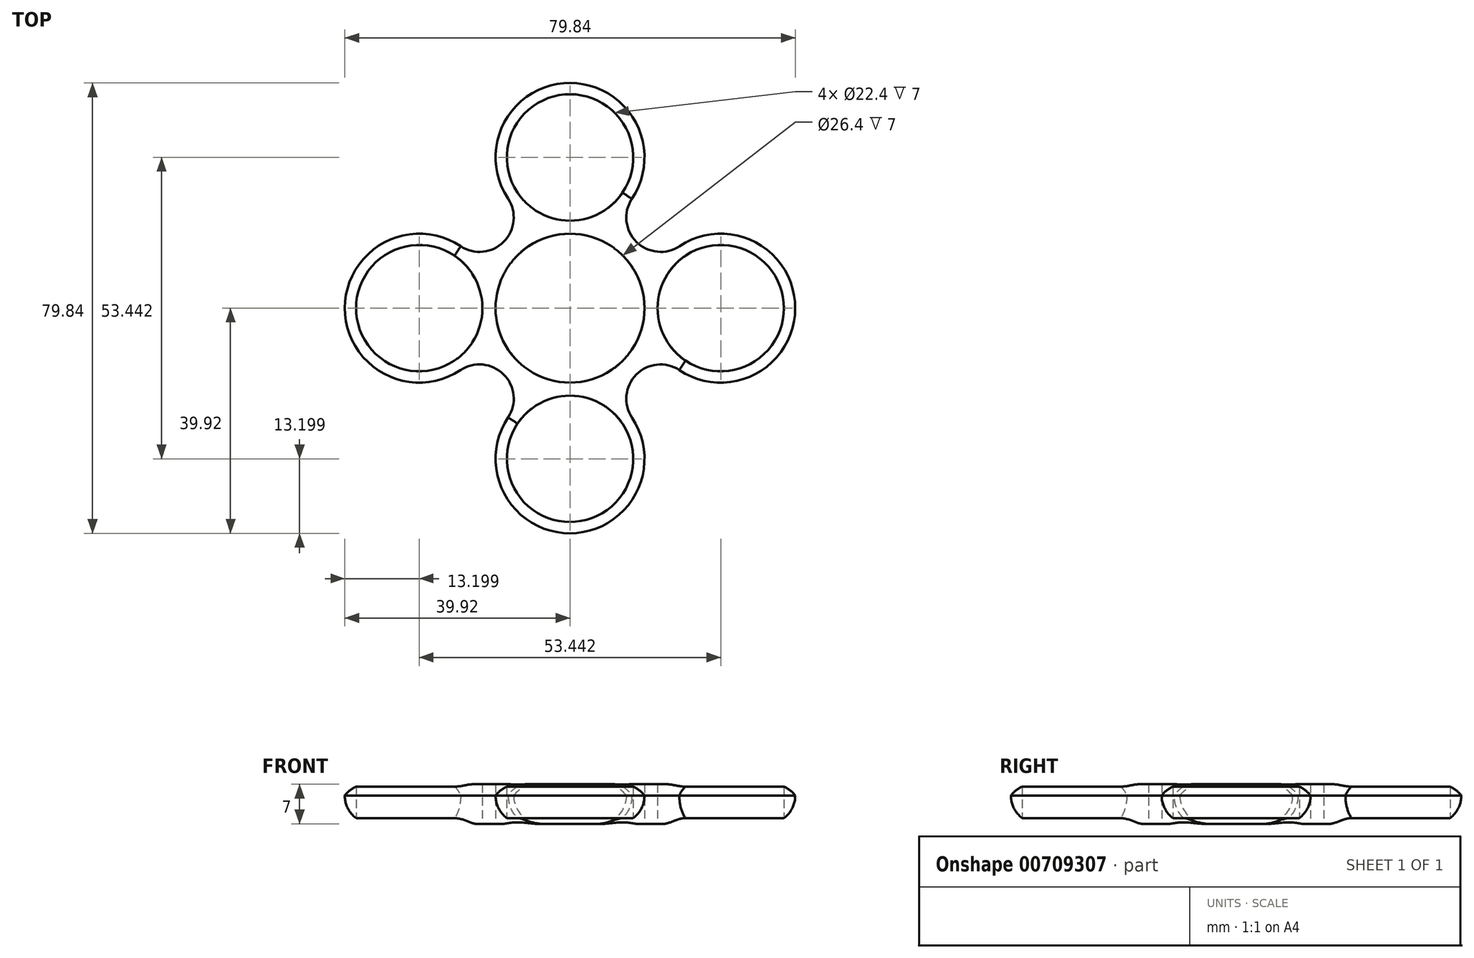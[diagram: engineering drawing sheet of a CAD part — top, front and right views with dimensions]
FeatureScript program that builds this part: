
annotation { "Feature Type Name" : "Feature", "Feature Type Description" : "" }
export const myFeature = defineFeature(function(context is Context, id is Id, definition is map)
    precondition{}
    {
        {
            var Q0;
            Q0=qCreatedBy(makeId("Top.planeOp"),FACE);
            var sketch = newSketch(context, id + "F0", { "sketchPlane" : qUnion([Q0])});
            skCircle(sketch, "E0", {"center": v(0, 0) * mm, "radius": 11.2 * mm});
            skCircle(sketch, "E1", {"center": v(0, 0) * mm, "radius": 13.2 * mm});
            skCircle(sketch, "E2", {"center": v(0, 26.72) * mm, "radius": 11.2 * mm});
            skArc(sketch, "E3", {"start": v(10.97, 19.37) * mm, "mid": v(0.02, 39.92) * mm, "end": v(-10.98, 19.4) * mm});
            skCircle(sketch, "E4.1.0", {"center": v(-26.72, 0) * mm, "radius": 11.2 * mm});
            skArc(sketch, "E4.1.1", {"start": v(-19.37, 10.97) * mm, "mid": v(-39.92, 0.02) * mm, "end": v(-19.4, -10.98) * mm});
            skCircle(sketch, "E4.2.0", {"center": v(0, -26.72) * mm, "radius": 11.2 * mm});
            skArc(sketch, "E4.2.1", {"start": v(-10.97, -19.37) * mm, "mid": v(-0.02, -39.92) * mm, "end": v(10.98, -19.4) * mm});
            skCircle(sketch, "E4.3.0", {"center": v(26.72, 0) * mm, "radius": 11.2 * mm});
            skArc(sketch, "E4.3.1", {"start": v(19.37, -10.97) * mm, "mid": v(39.92, -0.02) * mm, "end": v(19.4, 10.98) * mm});
            skArc(sketch, "E5", {"start": v(-19.37, 10.97) * mm, "mid": v(-11.73, 11.78) * mm, "end": v(-11, 19.43) * mm});
            skArc(sketch, "E6.1.0", {"start": v(-10.97, -19.37) * mm, "mid": v(-11.78, -11.73) * mm, "end": v(-19.43, -11) * mm});
            skArc(sketch, "E6.2.0", {"start": v(19.37, -10.97) * mm, "mid": v(11.73, -11.78) * mm, "end": v(11, -19.43) * mm});
            skArc(sketch, "E6.3.0", {"start": v(10.97, 19.37) * mm, "mid": v(11.78, 11.73) * mm, "end": v(19.43, 11) * mm});
            skSolve(sketch);
        }
        {
            var Q0;
            Q0=makeQuery(id+"F0.imprint","IMPRINT",FACE,{"disambiguationData":[TD([[makeQuery(id+"F0.imprint","IMPRINT",EDGE,{"derivedFrom":sQuery(id+"F0.wireOp",EDGE,"E1")}),-1.0]])]});
            extrude(context, id + "F1", {"entities" : qUnion([Q0]), "depth" : 7 * mm, "offsetDistance" : 25 * mm});
        }
        {
            var Q0;
            Q0=makeQuery(id+"F1.opExtrude","CAP_EDGE",EDGE,{"disambiguationData":[OSD([sQuery(id+"F0.wireOp",EDGE,"E4.3.1")])],"isStart":true});
            var Q1;
            Q1=makeQuery(id+"F1.opExtrude","CAP_EDGE",EDGE,{"disambiguationData":[OSD([sQuery(id+"F0.wireOp",EDGE,"E6.3.0")])],"isStart":true});
            var Q2;
            Q2=makeQuery(id+"F1.opExtrude","CAP_EDGE",EDGE,{"disambiguationData":[OSD([sQuery(id+"F0.wireOp",EDGE,"E3")])],"isStart":true});
            var Q3;
            Q3=makeQuery(id+"F1.opExtrude","CAP_EDGE",EDGE,{"disambiguationData":[OSD([sQuery(id+"F0.wireOp",EDGE,"E5")])],"isStart":true});
            var Q4;
            Q4=makeQuery(id+"F1.opExtrude","CAP_EDGE",EDGE,{"disambiguationData":[OSD([sQuery(id+"F0.wireOp",EDGE,"E4.1.1")])],"isStart":true});
            var Q5;
            Q5=makeQuery(id+"F1.opExtrude","CAP_EDGE",EDGE,{"disambiguationData":[OSD([sQuery(id+"F0.wireOp",EDGE,"E6.1.0")])],"isStart":true});
            var Q6;
            Q6=makeQuery(id+"F1.opExtrude","CAP_EDGE",EDGE,{"disambiguationData":[OSD([sQuery(id+"F0.wireOp",EDGE,"E4.2.1")])],"isStart":true});
            var Q7;
            Q7=makeQuery(id+"F1.opExtrude","CAP_EDGE",EDGE,{"disambiguationData":[OSD([sQuery(id+"F0.wireOp",EDGE,"E6.2.0")])],"isStart":true});
            fillet(context, id + "F2", {"entities" : qUnion([Q0, Q1, Q2, Q3, Q4, Q5, Q6, Q7]), "radius" : 5 * mm, "tangentPropagation" : true, "allowEdgeOverflow" : false});
        }
        {
            var Q0;
            Q0=makeQuery(id+"F1.opExtrude","CAP_EDGE",EDGE,{"disambiguationData":[OSD([sQuery(id+"F0.wireOp",EDGE,"E6.3.0")])],"isStart":false});
            var Q1;
            Q1=makeQuery(id+"F1.opExtrude","CAP_EDGE",EDGE,{"disambiguationData":[OSD([sQuery(id+"F0.wireOp",EDGE,"E5")])],"isStart":false});
            var Q2;
            Q2=makeQuery(id+"F1.opExtrude","CAP_EDGE",EDGE,{"disambiguationData":[OSD([sQuery(id+"F0.wireOp",EDGE,"E3")])],"isStart":false});
            var Q3;
            Q3=makeQuery(id+"F1.opExtrude","CAP_EDGE",EDGE,{"disambiguationData":[OSD([sQuery(id+"F0.wireOp",EDGE,"E6.2.0")])],"isStart":false});
            var Q4;
            Q4=makeQuery(id+"F1.opExtrude","CAP_EDGE",EDGE,{"disambiguationData":[OSD([sQuery(id+"F0.wireOp",EDGE,"E6.1.0")])],"isStart":false});
            var Q5;
            Q5=makeQuery(id+"F1.opExtrude","CAP_EDGE",EDGE,{"disambiguationData":[OSD([sQuery(id+"F0.wireOp",EDGE,"E4.3.1")])],"isStart":false});
            var Q6;
            Q6=makeQuery(id+"F1.opExtrude","CAP_EDGE",EDGE,{"disambiguationData":[OSD([sQuery(id+"F0.wireOp",EDGE,"E4.1.1")])],"isStart":false});
            var Q7;
            Q7=makeQuery(id+"F1.opExtrude","CAP_EDGE",EDGE,{"disambiguationData":[OSD([sQuery(id+"F0.wireOp",EDGE,"E4.2.1")])],"isStart":false});
            fillet(context, id + "F3", {"entities" : qUnion([Q0, Q1, Q2, Q3, Q4, Q5, Q6, Q7]), "radius" : 5 * mm, "tangentPropagation" : true, "allowEdgeOverflow" : false});
        }
    });
